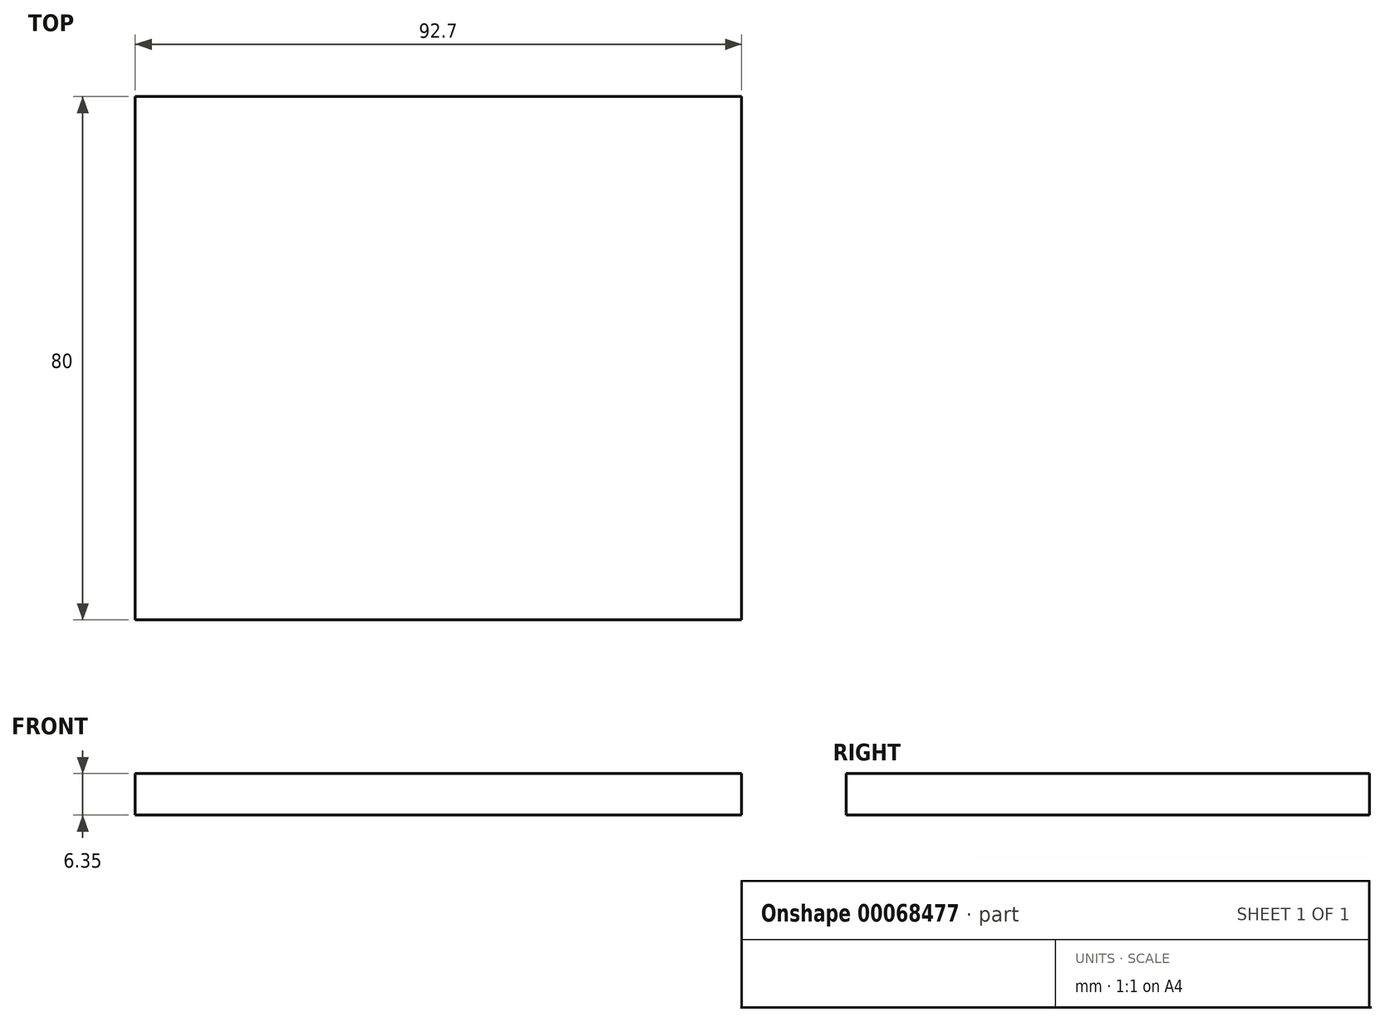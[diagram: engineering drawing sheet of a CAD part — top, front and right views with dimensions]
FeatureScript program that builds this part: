
annotation { "Feature Type Name" : "Feature", "Feature Type Description" : "" }
export const myFeature = defineFeature(function(context is Context, id is Id, definition is map)
    precondition{}
    {
        {
            var Q0;
            Q0=qCreatedBy(makeId("Top.planeOp"),FACE);
            var sketch = newSketch(context, id + "F0", { "sketchPlane" : qUnion([Q0])});
            skLineSegment(sketch, "E0.rect.bottom", {"start": v(46.35, 40) * mm, "end": v(-46.35, 40) * mm});
            skLineSegment(sketch, "E0.rect.top", {"start": v(46.35, -40) * mm, "end": v(-46.35, -40) * mm});
            skLineSegment(sketch, "E0.rect.left", {"start": v(46.35, 40) * mm, "end": v(46.35, -40) * mm});
            skLineSegment(sketch, "E0.rect.right", {"start": v(-46.35, 40) * mm, "end": v(-46.35, -40) * mm});
            skPoint(sketch, "E0.rect.middle", {"position": v(0, 0) * mm});
            skSolve(sketch);
        }
        {
            var Q0;
            Q0=makeQuery(id+"F0.imprint","IMPRINT",FACE,{"disambiguationData":[TD([[makeQuery(id+"F0.imprint","IMPRINT",EDGE,{"derivedFrom":sQuery(id+"F0.wireOp",EDGE,"E0.rect.bottom")}),1.0]])]});
            extrude(context, id + "F1", {"entities" : qUnion([Q0]), "depth" : 6.35 * mm});
        }
    });
